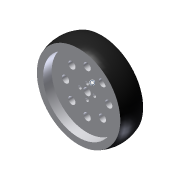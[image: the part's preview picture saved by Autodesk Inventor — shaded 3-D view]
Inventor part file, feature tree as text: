
AUTODESK INVENTOR PART (.ipt)
format: ipt  version: 2013 (Build 170138000, 138)  size: 148,992 bytes
history: native  units: in
note: dims shown in document units (in); Inventor stores cm internally (conversion verified against a paired STEP export)
features: other x1, imported_body x1, plane x1
ambient origin geometry x8: Origin, YZ Plane, XZ Plane, XY Plane, X Axis, Y Axis, Z Axis, Center Point
feature tree (3):
  other  "WHEEL_101MM_4-IN_2011"
  imported_body  "Base1"
  plane  "Work Plane1"
